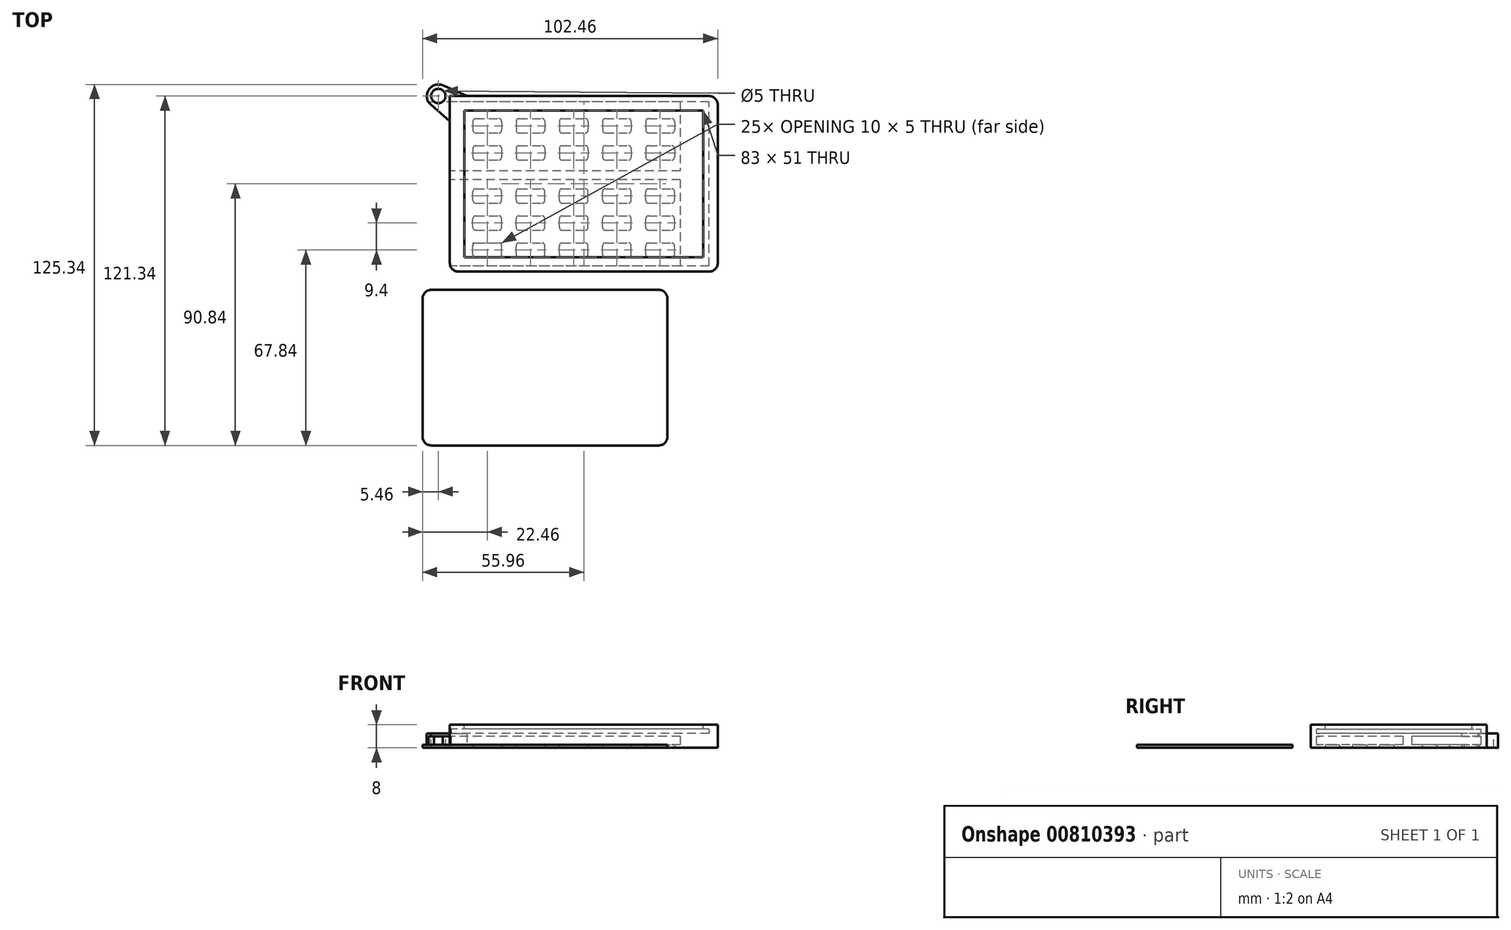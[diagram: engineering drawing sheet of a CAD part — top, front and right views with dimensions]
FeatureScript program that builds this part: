
annotation { "Feature Type Name" : "Feature", "Feature Type Description" : "" }
export const myFeature = defineFeature(function(context is Context, id is Id, definition is map)
    precondition{}
    {
        {
            var Q0;
            Q0=qCreatedBy(makeId("Top.planeOp"),FACE);
            var sketch = newSketch(context, id + "F0", { "sketchPlane" : qUnion([Q0])});
            skLineSegment(sketch, "E0.bottom", {"start": v(0, 0) * mm, "end": v(93, 0) * mm});
            skLineSegment(sketch, "E0.top", {"start": v(0, 61) * mm, "end": v(93, 61) * mm});
            skLineSegment(sketch, "E0.left", {"start": v(0, 0) * mm, "end": v(0, 61) * mm});
            skLineSegment(sketch, "E0.right", {"start": v(93, 0) * mm, "end": v(93, 61) * mm});
            skSolve(sketch);
        }
        {
            var Q0;
            Q0 = qSketchRegion(id + "F0", true);
            extrude(context, id + "F1", {"entities" : qUnion([Q0]), "depth" : 8 * mm, "offsetDistance" : 25 * mm});
        }
        {
            var Q0;
            Q0=makeQuery(id+"F1.opExtrude","SWEPT_EDGE",EDGE,{"disambiguationData":[OSD([sQuery(id+"F0.wireOp",EDGE,"E0.bottom"),sQuery(id+"F0.wireOp",EDGE,"E0.right")])]});
            var Q1;
            Q1=makeQuery(id+"F1.opExtrude","SWEPT_EDGE",EDGE,{"disambiguationData":[OSD([sQuery(id+"F0.wireOp",EDGE,"E0.top"),sQuery(id+"F0.wireOp",EDGE,"E0.right")])]});
            var Q2;
            Q2=makeQuery(id+"F1.opExtrude","SWEPT_EDGE",EDGE,{"disambiguationData":[OSD([sQuery(id+"F0.wireOp",EDGE,"E0.bottom"),sQuery(id+"F0.wireOp",EDGE,"E0.left")])]});
            fillet(context, id + "F2", {"entities" : qUnion([Q0, Q1, Q2]), "radius" : 3 * mm, "tangentPropagation" : true, "allowEdgeOverflow" : false});
        }
        {
            var Q0;
            Q0=qCreatedBy(makeId("Right.planeOp"),FACE);
            var sketch = newSketch(context, id + "F3", { "sketchPlane" : qUnion([Q0])});
            skLineSegment(sketch, "E1.bottom", {"start": v(2, 6.5) * mm, "end": v(59, 6.5) * mm});
            skLineSegment(sketch, "E1.top", {"start": v(59, 5) * mm, "end": v(2, 5) * mm});
            skLineSegment(sketch, "E1.left", {"start": v(59, 6.5) * mm, "end": v(59, 5) * mm});
            skLineSegment(sketch, "E1.right", {"start": v(2, 6.5) * mm, "end": v(2, 5) * mm});
            skLineSegment(sketch, "E2", {"start": v(30.5, 26.88) * mm, "end": v(30.5, -6.88) * mm, "construction": true});
            skSolve(sketch);
        }
        {
            var Q0;
            Q0 = qSketchRegion(id + "F3", true);
            extrude(context, id + "F4", {"entities" : qUnion([Q0]), "operationType" : NewBodyOperationType.REMOVE, "depth" : 90 * mm, "offsetDistance" : 25 * mm});
        }
        {
            var Q0;
            Q0=makeQuery(id+"F1.opExtrude","CAP_FACE",FACE,{"disambiguationData":[OSD([sQuery(id+"F0.wireOp",EDGE,"E0.bottom"),sQuery(id+"F0.wireOp",EDGE,"E0.top"),sQuery(id+"F0.wireOp",EDGE,"E0.left"),sQuery(id+"F0.wireOp",EDGE,"E0.right")])],"isStart":false});
            var sketch = newSketch(context, id + "F5", { "sketchPlane" : qUnion([Q0])});
            skLineSegment(sketch, "E3.bottom", {"start": v(5, 56) * mm, "end": v(88, 56) * mm});
            skLineSegment(sketch, "E3.top", {"start": v(5, 5) * mm, "end": v(88, 5) * mm});
            skLineSegment(sketch, "E3.left", {"start": v(5, 56) * mm, "end": v(5, 5) * mm});
            skLineSegment(sketch, "E3.right", {"start": v(88, 56) * mm, "end": v(88, 5) * mm});
            skSolve(sketch);
        }
        {
            var Q0;
            Q0 = qSketchRegion(id + "F5", true);
            extrude(context, id + "F6", {"entities" : qUnion([Q0]), "operationType" : NewBodyOperationType.REMOVE, "endBound" : BoundingType.UP_TO_NEXT, "oppositeDirection" : true, "depth" : 25 * mm, "offsetDistance" : 25 * mm, "hasSecondDirection" : true, "secondDirectionOppositeDirection" : false, "secondDirectionDepth" : 25 * mm});
        }
        {
            var Q0;
            Q0=makeQuery(id+"F1.opExtrude","SWEPT_FACE",FACE,{"disambiguationData":[OSD([sQuery(id+"F0.wireOp",EDGE,"E0.left")])]});
            var sketch = newSketch(context, id + "F7", { "sketchPlane" : qUnion([Q0])});
            skLineSegment(sketch, "E4.bottom", {"start": v(-32, 4) * mm, "end": v(-2, 4) * mm});
            skLineSegment(sketch, "E4.top", {"start": v(-32, 1) * mm, "end": v(-2, 1) * mm});
            skLineSegment(sketch, "E4.left", {"start": v(-32, 4) * mm, "end": v(-32, 1) * mm});
            skLineSegment(sketch, "E4.right", {"start": v(-2, 4) * mm, "end": v(-2, 1) * mm});
            skLineSegment(sketch, "E5.bottom", {"start": v(-59, 4) * mm, "end": v(-35, 4) * mm});
            skLineSegment(sketch, "E5.top", {"start": v(-59, 1) * mm, "end": v(-35, 1) * mm});
            skLineSegment(sketch, "E5.left", {"start": v(-59, 4) * mm, "end": v(-59, 1) * mm});
            skLineSegment(sketch, "E5.right", {"start": v(-35, 4) * mm, "end": v(-35, 1) * mm});
            skSolve(sketch);
        }
        {
            var Q0;
            Q0 = qSketchRegion(id + "F7", true);
            extrude(context, id + "F8", {"entities" : qUnion([Q0]), "operationType" : NewBodyOperationType.REMOVE, "oppositeDirection" : true, "depth" : 80 * mm, "offsetDistance" : 25 * mm});
        }
        {
            var Q0;
            Q0=makeQuery(id+"F1.opExtrude","CAP_FACE",FACE,{"disambiguationData":[OSD([sQuery(id+"F0.wireOp",EDGE,"E0.bottom"),sQuery(id+"F0.wireOp",EDGE,"E0.top"),sQuery(id+"F0.wireOp",EDGE,"E0.left"),sQuery(id+"F0.wireOp",EDGE,"E0.right")])],"isStart":true});
            var sketch = newSketch(context, id + "F9", { "sketchPlane" : qUnion([Q0])});
            skLineSegment(sketch, "E6.bottom", {"start": v(9, -5) * mm, "end": v(17, -5) * mm});
            skLineSegment(sketch, "E6.top", {"start": v(9, -10) * mm, "end": v(17, -10) * mm});
            skLineSegment(sketch, "E6.left", {"start": v(8, -6) * mm, "end": v(8, -9) * mm});
            skLineSegment(sketch, "E6.right", {"start": v(18, -6) * mm, "end": v(18, -9) * mm});
            skLineSegment(sketch, "E7", {"start": v(46.5, 0) * mm, "end": v(46.5, -63.42) * mm, "construction": true});
            skPoint(sketch, "E8.visualSharp", {"position": v(18, -10) * mm});
            skArc(sketch, "E8.filletArc", {"start": v(17, -10) * mm, "mid": v(17.7, -9.7) * mm, "end": v(18, -9) * mm});
            skPoint(sketch, "E9.visualSharp", {"position": v(18, -5) * mm});
            skArc(sketch, "E9.filletArc", {"start": v(18, -6) * mm, "mid": v(17.7, -5.3) * mm, "end": v(17, -5) * mm});
            skPoint(sketch, "E10.visualSharp", {"position": v(8, -10) * mm});
            skArc(sketch, "E10.filletArc", {"start": v(8, -9) * mm, "mid": v(8.3, -9.7) * mm, "end": v(9, -10) * mm});
            skPoint(sketch, "E11.visualSharp", {"position": v(8, -5) * mm});
            skArc(sketch, "E11.filletArc", {"start": v(9, -5) * mm, "mid": v(8.3, -5.3) * mm, "end": v(8, -6) * mm});
            skPoint(sketch, "E12.0.1.0", {"position": v(8, -14.4) * mm});
            skLineSegment(sketch, "E12.0.1.1", {"start": v(9, -14.4) * mm, "end": v(17, -14.4) * mm});
            skPoint(sketch, "E12.0.1.2", {"position": v(8, -19.4) * mm});
            skLineSegment(sketch, "E12.0.1.3", {"start": v(8, -15.4) * mm, "end": v(8, -18.4) * mm});
            skPoint(sketch, "E12.0.1.4", {"position": v(18, -19.4) * mm});
            skLineSegment(sketch, "E12.0.1.5", {"start": v(9, -19.4) * mm, "end": v(17, -19.4) * mm});
            skPoint(sketch, "E12.0.1.6", {"position": v(18, -14.4) * mm});
            skLineSegment(sketch, "E12.0.1.7", {"start": v(18, -15.4) * mm, "end": v(18, -18.4) * mm});
            skArc(sketch, "E12.0.1.8", {"start": v(17, -19.4) * mm, "mid": v(17.7, -19.1) * mm, "end": v(18, -18.4) * mm});
            skArc(sketch, "E12.0.1.9", {"start": v(9, -14.4) * mm, "mid": v(8.3, -14.7) * mm, "end": v(8, -15.4) * mm});
            skArc(sketch, "E12.0.1.10", {"start": v(18, -15.4) * mm, "mid": v(17.7, -14.7) * mm, "end": v(17, -14.4) * mm});
            skArc(sketch, "E12.0.1.11", {"start": v(8, -18.4) * mm, "mid": v(8.3, -19.1) * mm, "end": v(9, -19.4) * mm});
            skPoint(sketch, "E12.0.2.0", {"position": v(8, -23.8) * mm});
            skLineSegment(sketch, "E12.0.2.1", {"start": v(9, -23.8) * mm, "end": v(17, -23.8) * mm});
            skPoint(sketch, "E12.0.2.2", {"position": v(8, -28.8) * mm});
            skLineSegment(sketch, "E12.0.2.3", {"start": v(8, -24.8) * mm, "end": v(8, -27.8) * mm});
            skPoint(sketch, "E12.0.2.4", {"position": v(18, -28.8) * mm});
            skLineSegment(sketch, "E12.0.2.5", {"start": v(9, -28.8) * mm, "end": v(17, -28.8) * mm});
            skPoint(sketch, "E12.0.2.6", {"position": v(18, -23.8) * mm});
            skLineSegment(sketch, "E12.0.2.7", {"start": v(18, -24.8) * mm, "end": v(18, -27.8) * mm});
            skArc(sketch, "E12.0.2.8", {"start": v(17, -28.8) * mm, "mid": v(17.7, -28.5) * mm, "end": v(18, -27.8) * mm});
            skArc(sketch, "E12.0.2.9", {"start": v(9, -23.8) * mm, "mid": v(8.3, -24.1) * mm, "end": v(8, -24.8) * mm});
            skArc(sketch, "E12.0.2.10", {"start": v(18, -24.8) * mm, "mid": v(17.7, -24.1) * mm, "end": v(17, -23.8) * mm});
            skArc(sketch, "E12.0.2.11", {"start": v(8, -27.8) * mm, "mid": v(8.3, -28.5) * mm, "end": v(9, -28.8) * mm});
            skPoint(sketch, "E12.1.0.0", {"position": v(23, -5) * mm});
            skLineSegment(sketch, "E12.1.0.1", {"start": v(24, -5) * mm, "end": v(32, -5) * mm});
            skPoint(sketch, "E12.1.0.2", {"position": v(23, -10) * mm});
            skLineSegment(sketch, "E12.1.0.3", {"start": v(23, -6) * mm, "end": v(23, -9) * mm});
            skPoint(sketch, "E12.1.0.4", {"position": v(33, -10) * mm});
            skLineSegment(sketch, "E12.1.0.5", {"start": v(24, -10) * mm, "end": v(32, -10) * mm});
            skPoint(sketch, "E12.1.0.6", {"position": v(33, -5) * mm});
            skLineSegment(sketch, "E12.1.0.7", {"start": v(33, -6) * mm, "end": v(33, -9) * mm});
            skArc(sketch, "E12.1.0.8", {"start": v(32, -10) * mm, "mid": v(32.7, -9.7) * mm, "end": v(33, -9) * mm});
            skArc(sketch, "E12.1.0.9", {"start": v(24, -5) * mm, "mid": v(23.3, -5.3) * mm, "end": v(23, -6) * mm});
            skArc(sketch, "E12.1.0.10", {"start": v(33, -6) * mm, "mid": v(32.7, -5.3) * mm, "end": v(32, -5) * mm});
            skArc(sketch, "E12.1.0.11", {"start": v(23, -9) * mm, "mid": v(23.3, -9.7) * mm, "end": v(24, -10) * mm});
            skPoint(sketch, "E12.1.1.0", {"position": v(23, -14.4) * mm});
            skLineSegment(sketch, "E12.1.1.1", {"start": v(24, -14.4) * mm, "end": v(32, -14.4) * mm});
            skPoint(sketch, "E12.1.1.2", {"position": v(23, -19.4) * mm});
            skLineSegment(sketch, "E12.1.1.3", {"start": v(23, -15.4) * mm, "end": v(23, -18.4) * mm});
            skPoint(sketch, "E12.1.1.4", {"position": v(33, -19.4) * mm});
            skLineSegment(sketch, "E12.1.1.5", {"start": v(24, -19.4) * mm, "end": v(32, -19.4) * mm});
            skPoint(sketch, "E12.1.1.6", {"position": v(33, -14.4) * mm});
            skLineSegment(sketch, "E12.1.1.7", {"start": v(33, -15.4) * mm, "end": v(33, -18.4) * mm});
            skArc(sketch, "E12.1.1.8", {"start": v(32, -19.4) * mm, "mid": v(32.7, -19.1) * mm, "end": v(33, -18.4) * mm});
            skArc(sketch, "E12.1.1.9", {"start": v(24, -14.4) * mm, "mid": v(23.3, -14.7) * mm, "end": v(23, -15.4) * mm});
            skArc(sketch, "E12.1.1.10", {"start": v(33, -15.4) * mm, "mid": v(32.7, -14.7) * mm, "end": v(32, -14.4) * mm});
            skArc(sketch, "E12.1.1.11", {"start": v(23, -18.4) * mm, "mid": v(23.3, -19.1) * mm, "end": v(24, -19.4) * mm});
            skPoint(sketch, "E12.1.2.0", {"position": v(23, -23.8) * mm});
            skLineSegment(sketch, "E12.1.2.1", {"start": v(24, -23.8) * mm, "end": v(32, -23.8) * mm});
            skPoint(sketch, "E12.1.2.2", {"position": v(23, -28.8) * mm});
            skLineSegment(sketch, "E12.1.2.3", {"start": v(23, -24.8) * mm, "end": v(23, -27.8) * mm});
            skPoint(sketch, "E12.1.2.4", {"position": v(33, -28.8) * mm});
            skLineSegment(sketch, "E12.1.2.5", {"start": v(24, -28.8) * mm, "end": v(32, -28.8) * mm});
            skPoint(sketch, "E12.1.2.6", {"position": v(33, -23.8) * mm});
            skLineSegment(sketch, "E12.1.2.7", {"start": v(33, -24.8) * mm, "end": v(33, -27.8) * mm});
            skArc(sketch, "E12.1.2.8", {"start": v(32, -28.8) * mm, "mid": v(32.7, -28.5) * mm, "end": v(33, -27.8) * mm});
            skArc(sketch, "E12.1.2.9", {"start": v(24, -23.8) * mm, "mid": v(23.3, -24.1) * mm, "end": v(23, -24.8) * mm});
            skArc(sketch, "E12.1.2.10", {"start": v(33, -24.8) * mm, "mid": v(32.7, -24.1) * mm, "end": v(32, -23.8) * mm});
            skArc(sketch, "E12.1.2.11", {"start": v(23, -27.8) * mm, "mid": v(23.3, -28.5) * mm, "end": v(24, -28.8) * mm});
            skPoint(sketch, "E12.2.0.0", {"position": v(38, -5) * mm});
            skLineSegment(sketch, "E12.2.0.1", {"start": v(39, -5) * mm, "end": v(47, -5) * mm});
            skPoint(sketch, "E12.2.0.2", {"position": v(38, -10) * mm});
            skLineSegment(sketch, "E12.2.0.3", {"start": v(38, -6) * mm, "end": v(38, -9) * mm});
            skPoint(sketch, "E12.2.0.4", {"position": v(48, -10) * mm});
            skLineSegment(sketch, "E12.2.0.5", {"start": v(39, -10) * mm, "end": v(47, -10) * mm});
            skPoint(sketch, "E12.2.0.6", {"position": v(48, -5) * mm});
            skLineSegment(sketch, "E12.2.0.7", {"start": v(48, -6) * mm, "end": v(48, -9) * mm});
            skArc(sketch, "E12.2.0.8", {"start": v(47, -10) * mm, "mid": v(47.7, -9.7) * mm, "end": v(48, -9) * mm});
            skArc(sketch, "E12.2.0.9", {"start": v(39, -5) * mm, "mid": v(38.3, -5.3) * mm, "end": v(38, -6) * mm});
            skArc(sketch, "E12.2.0.10", {"start": v(48, -6) * mm, "mid": v(47.7, -5.3) * mm, "end": v(47, -5) * mm});
            skArc(sketch, "E12.2.0.11", {"start": v(38, -9) * mm, "mid": v(38.3, -9.7) * mm, "end": v(39, -10) * mm});
            skPoint(sketch, "E12.2.1.0", {"position": v(38, -14.4) * mm});
            skLineSegment(sketch, "E12.2.1.1", {"start": v(39, -14.4) * mm, "end": v(47, -14.4) * mm});
            skPoint(sketch, "E12.2.1.2", {"position": v(38, -19.4) * mm});
            skLineSegment(sketch, "E12.2.1.3", {"start": v(38, -15.4) * mm, "end": v(38, -18.4) * mm});
            skPoint(sketch, "E12.2.1.4", {"position": v(48, -19.4) * mm});
            skLineSegment(sketch, "E12.2.1.5", {"start": v(39, -19.4) * mm, "end": v(47, -19.4) * mm});
            skPoint(sketch, "E12.2.1.6", {"position": v(48, -14.4) * mm});
            skLineSegment(sketch, "E12.2.1.7", {"start": v(48, -15.4) * mm, "end": v(48, -18.4) * mm});
            skArc(sketch, "E12.2.1.8", {"start": v(47, -19.4) * mm, "mid": v(47.7, -19.1) * mm, "end": v(48, -18.4) * mm});
            skArc(sketch, "E12.2.1.9", {"start": v(39, -14.4) * mm, "mid": v(38.3, -14.7) * mm, "end": v(38, -15.4) * mm});
            skArc(sketch, "E12.2.1.10", {"start": v(48, -15.4) * mm, "mid": v(47.7, -14.7) * mm, "end": v(47, -14.4) * mm});
            skArc(sketch, "E12.2.1.11", {"start": v(38, -18.4) * mm, "mid": v(38.3, -19.1) * mm, "end": v(39, -19.4) * mm});
            skPoint(sketch, "E12.2.2.0", {"position": v(38, -23.8) * mm});
            skLineSegment(sketch, "E12.2.2.1", {"start": v(39, -23.8) * mm, "end": v(47, -23.8) * mm});
            skPoint(sketch, "E12.2.2.2", {"position": v(38, -28.8) * mm});
            skLineSegment(sketch, "E12.2.2.3", {"start": v(38, -24.8) * mm, "end": v(38, -27.8) * mm});
            skPoint(sketch, "E12.2.2.4", {"position": v(48, -28.8) * mm});
            skLineSegment(sketch, "E12.2.2.5", {"start": v(39, -28.8) * mm, "end": v(47, -28.8) * mm});
            skPoint(sketch, "E12.2.2.6", {"position": v(48, -23.8) * mm});
            skLineSegment(sketch, "E12.2.2.7", {"start": v(48, -24.8) * mm, "end": v(48, -27.8) * mm});
            skArc(sketch, "E12.2.2.8", {"start": v(47, -28.8) * mm, "mid": v(47.7, -28.5) * mm, "end": v(48, -27.8) * mm});
            skArc(sketch, "E12.2.2.9", {"start": v(39, -23.8) * mm, "mid": v(38.3, -24.1) * mm, "end": v(38, -24.8) * mm});
            skArc(sketch, "E12.2.2.10", {"start": v(48, -24.8) * mm, "mid": v(47.7, -24.1) * mm, "end": v(47, -23.8) * mm});
            skArc(sketch, "E12.2.2.11", {"start": v(38, -27.8) * mm, "mid": v(38.3, -28.5) * mm, "end": v(39, -28.8) * mm});
            skPoint(sketch, "E12.3.0.0", {"position": v(53, -5) * mm});
            skLineSegment(sketch, "E12.3.0.1", {"start": v(54, -5) * mm, "end": v(62, -5) * mm});
            skPoint(sketch, "E12.3.0.2", {"position": v(53, -10) * mm});
            skLineSegment(sketch, "E12.3.0.3", {"start": v(53, -6) * mm, "end": v(53, -9) * mm});
            skPoint(sketch, "E12.3.0.4", {"position": v(63, -10) * mm});
            skLineSegment(sketch, "E12.3.0.5", {"start": v(54, -10) * mm, "end": v(62, -10) * mm});
            skPoint(sketch, "E12.3.0.6", {"position": v(63, -5) * mm});
            skLineSegment(sketch, "E12.3.0.7", {"start": v(63, -6) * mm, "end": v(63, -9) * mm});
            skArc(sketch, "E12.3.0.8", {"start": v(62, -10) * mm, "mid": v(62.7, -9.7) * mm, "end": v(63, -9) * mm});
            skArc(sketch, "E12.3.0.9", {"start": v(54, -5) * mm, "mid": v(53.3, -5.3) * mm, "end": v(53, -6) * mm});
            skArc(sketch, "E12.3.0.10", {"start": v(63, -6) * mm, "mid": v(62.7, -5.3) * mm, "end": v(62, -5) * mm});
            skArc(sketch, "E12.3.0.11", {"start": v(53, -9) * mm, "mid": v(53.3, -9.7) * mm, "end": v(54, -10) * mm});
            skPoint(sketch, "E12.3.1.0", {"position": v(53, -14.4) * mm});
            skLineSegment(sketch, "E12.3.1.1", {"start": v(54, -14.4) * mm, "end": v(62, -14.4) * mm});
            skPoint(sketch, "E12.3.1.2", {"position": v(53, -19.4) * mm});
            skLineSegment(sketch, "E12.3.1.3", {"start": v(53, -15.4) * mm, "end": v(53, -18.4) * mm});
            skPoint(sketch, "E12.3.1.4", {"position": v(63, -19.4) * mm});
            skLineSegment(sketch, "E12.3.1.5", {"start": v(54, -19.4) * mm, "end": v(62, -19.4) * mm});
            skPoint(sketch, "E12.3.1.6", {"position": v(63, -14.4) * mm});
            skLineSegment(sketch, "E12.3.1.7", {"start": v(63, -15.4) * mm, "end": v(63, -18.4) * mm});
            skArc(sketch, "E12.3.1.8", {"start": v(62, -19.4) * mm, "mid": v(62.7, -19.1) * mm, "end": v(63, -18.4) * mm});
            skArc(sketch, "E12.3.1.9", {"start": v(54, -14.4) * mm, "mid": v(53.3, -14.7) * mm, "end": v(53, -15.4) * mm});
            skArc(sketch, "E12.3.1.10", {"start": v(63, -15.4) * mm, "mid": v(62.7, -14.7) * mm, "end": v(62, -14.4) * mm});
            skArc(sketch, "E12.3.1.11", {"start": v(53, -18.4) * mm, "mid": v(53.3, -19.1) * mm, "end": v(54, -19.4) * mm});
            skPoint(sketch, "E12.3.2.0", {"position": v(53, -23.8) * mm});
            skLineSegment(sketch, "E12.3.2.1", {"start": v(54, -23.8) * mm, "end": v(62, -23.8) * mm});
            skPoint(sketch, "E12.3.2.2", {"position": v(53, -28.8) * mm});
            skLineSegment(sketch, "E12.3.2.3", {"start": v(53, -24.8) * mm, "end": v(53, -27.8) * mm});
            skPoint(sketch, "E12.3.2.4", {"position": v(63, -28.8) * mm});
            skLineSegment(sketch, "E12.3.2.5", {"start": v(54, -28.8) * mm, "end": v(62, -28.8) * mm});
            skPoint(sketch, "E12.3.2.6", {"position": v(63, -23.8) * mm});
            skLineSegment(sketch, "E12.3.2.7", {"start": v(63, -24.8) * mm, "end": v(63, -27.8) * mm});
            skArc(sketch, "E12.3.2.8", {"start": v(62, -28.8) * mm, "mid": v(62.7, -28.5) * mm, "end": v(63, -27.8) * mm});
            skArc(sketch, "E12.3.2.9", {"start": v(54, -23.8) * mm, "mid": v(53.3, -24.1) * mm, "end": v(53, -24.8) * mm});
            skArc(sketch, "E12.3.2.10", {"start": v(63, -24.8) * mm, "mid": v(62.7, -24.1) * mm, "end": v(62, -23.8) * mm});
            skArc(sketch, "E12.3.2.11", {"start": v(53, -27.8) * mm, "mid": v(53.3, -28.5) * mm, "end": v(54, -28.8) * mm});
            skPoint(sketch, "E12.4.0.0", {"position": v(68, -5) * mm});
            skLineSegment(sketch, "E12.4.0.1", {"start": v(69, -5) * mm, "end": v(77, -5) * mm});
            skPoint(sketch, "E12.4.0.2", {"position": v(68, -10) * mm});
            skLineSegment(sketch, "E12.4.0.3", {"start": v(68, -6) * mm, "end": v(68, -9) * mm});
            skPoint(sketch, "E12.4.0.4", {"position": v(78, -10) * mm});
            skLineSegment(sketch, "E12.4.0.5", {"start": v(69, -10) * mm, "end": v(77, -10) * mm});
            skPoint(sketch, "E12.4.0.6", {"position": v(78, -5) * mm});
            skLineSegment(sketch, "E12.4.0.7", {"start": v(78, -6) * mm, "end": v(78, -9) * mm});
            skArc(sketch, "E12.4.0.8", {"start": v(77, -10) * mm, "mid": v(77.7, -9.7) * mm, "end": v(78, -9) * mm});
            skArc(sketch, "E12.4.0.9", {"start": v(69, -5) * mm, "mid": v(68.3, -5.3) * mm, "end": v(68, -6) * mm});
            skArc(sketch, "E12.4.0.10", {"start": v(78, -6) * mm, "mid": v(77.7, -5.3) * mm, "end": v(77, -5) * mm});
            skArc(sketch, "E12.4.0.11", {"start": v(68, -9) * mm, "mid": v(68.3, -9.7) * mm, "end": v(69, -10) * mm});
            skPoint(sketch, "E12.4.1.0", {"position": v(68, -14.4) * mm});
            skLineSegment(sketch, "E12.4.1.1", {"start": v(69, -14.4) * mm, "end": v(77, -14.4) * mm});
            skPoint(sketch, "E12.4.1.2", {"position": v(68, -19.4) * mm});
            skLineSegment(sketch, "E12.4.1.3", {"start": v(68, -15.4) * mm, "end": v(68, -18.4) * mm});
            skPoint(sketch, "E12.4.1.4", {"position": v(78, -19.4) * mm});
            skLineSegment(sketch, "E12.4.1.5", {"start": v(69, -19.4) * mm, "end": v(77, -19.4) * mm});
            skPoint(sketch, "E12.4.1.6", {"position": v(78, -14.4) * mm});
            skLineSegment(sketch, "E12.4.1.7", {"start": v(78, -15.4) * mm, "end": v(78, -18.4) * mm});
            skArc(sketch, "E12.4.1.8", {"start": v(77, -19.4) * mm, "mid": v(77.7, -19.1) * mm, "end": v(78, -18.4) * mm});
            skArc(sketch, "E12.4.1.9", {"start": v(69, -14.4) * mm, "mid": v(68.3, -14.7) * mm, "end": v(68, -15.4) * mm});
            skArc(sketch, "E12.4.1.10", {"start": v(78, -15.4) * mm, "mid": v(77.7, -14.7) * mm, "end": v(77, -14.4) * mm});
            skArc(sketch, "E12.4.1.11", {"start": v(68, -18.4) * mm, "mid": v(68.3, -19.1) * mm, "end": v(69, -19.4) * mm});
            skPoint(sketch, "E12.4.2.0", {"position": v(68, -23.8) * mm});
            skLineSegment(sketch, "E12.4.2.1", {"start": v(69, -23.8) * mm, "end": v(77, -23.8) * mm});
            skPoint(sketch, "E12.4.2.2", {"position": v(68, -28.8) * mm});
            skLineSegment(sketch, "E12.4.2.3", {"start": v(68, -24.8) * mm, "end": v(68, -27.8) * mm});
            skPoint(sketch, "E12.4.2.4", {"position": v(78, -28.8) * mm});
            skLineSegment(sketch, "E12.4.2.5", {"start": v(69, -28.8) * mm, "end": v(77, -28.8) * mm});
            skPoint(sketch, "E12.4.2.6", {"position": v(78, -23.8) * mm});
            skLineSegment(sketch, "E12.4.2.7", {"start": v(78, -24.8) * mm, "end": v(78, -27.8) * mm});
            skArc(sketch, "E12.4.2.8", {"start": v(77, -28.8) * mm, "mid": v(77.7, -28.5) * mm, "end": v(78, -27.8) * mm});
            skArc(sketch, "E12.4.2.9", {"start": v(69, -23.8) * mm, "mid": v(68.3, -24.1) * mm, "end": v(68, -24.8) * mm});
            skArc(sketch, "E12.4.2.10", {"start": v(78, -24.8) * mm, "mid": v(77.7, -24.1) * mm, "end": v(77, -23.8) * mm});
            skArc(sketch, "E12.4.2.11", {"start": v(68, -27.8) * mm, "mid": v(68.3, -28.5) * mm, "end": v(69, -28.8) * mm});
            skLineSegment(sketch, "E12.direction1", {"start": v(8, -10) * mm, "end": v(23, -10) * mm, "construction": true});
            skLineSegment(sketch, "E12.direction2", {"start": v(8, -10) * mm, "end": v(8, -19.4) * mm, "construction": true});
            skLineSegment(sketch, "E13", {"start": v(0, -33.78) * mm, "end": v(93, -33.78) * mm, "construction": true});
            skLineSegment(sketch, "E14.MirrorCS", {"start": v(23, -52.16) * mm, "end": v(23, -49.16) * mm});
            skArc(sketch, "E15.MirrorCS", {"start": v(78, -52.16) * mm, "mid": v(77.7, -52.86) * mm, "end": v(77, -53.16) * mm});
            skArc(sketch, "E16.MirrorCS", {"start": v(48, -52.16) * mm, "mid": v(47.7, -52.86) * mm, "end": v(47, -53.16) * mm});
            skArc(sketch, "E17.MirrorCS", {"start": v(69, -53.16) * mm, "mid": v(68.3, -52.86) * mm, "end": v(68, -52.16) * mm});
            skArc(sketch, "E18.MirrorCS", {"start": v(39, -53.16) * mm, "mid": v(38.3, -52.86) * mm, "end": v(38, -52.16) * mm});
            skArc(sketch, "E19.MirrorCS", {"start": v(62, -38.76) * mm, "mid": v(62.7, -39.05) * mm, "end": v(63, -39.76) * mm});
            skLineSegment(sketch, "E20.MirrorCS", {"start": v(8, -52.16) * mm, "end": v(8, -49.16) * mm});
            skArc(sketch, "E21.MirrorCS", {"start": v(9, -53.16) * mm, "mid": v(8.3, -52.86) * mm, "end": v(8, -52.16) * mm});
            skArc(sketch, "E22.MirrorCS", {"start": v(24, -53.16) * mm, "mid": v(23.3, -52.86) * mm, "end": v(23, -52.16) * mm});
            skArc(sketch, "E23.MirrorCS", {"start": v(9, -43.76) * mm, "mid": v(8.3, -43.46) * mm, "end": v(8, -42.76) * mm});
            skLineSegment(sketch, "E24.MirrorCS", {"start": v(68, -42.76) * mm, "end": v(68, -39.76) * mm});
            skLineSegment(sketch, "E25.MirrorCS", {"start": v(38, -42.76) * mm, "end": v(38, -39.76) * mm});
            skLineSegment(sketch, "E26.MirrorCS", {"start": v(53, -52.16) * mm, "end": v(53, -49.16) * mm});
            skLineSegment(sketch, "E27.MirrorCS", {"start": v(8, -42.76) * mm, "end": v(8, -39.76) * mm});
            skArc(sketch, "E28.MirrorCS", {"start": v(53, -39.76) * mm, "mid": v(53.3, -39.05) * mm, "end": v(54, -38.76) * mm});
            skArc(sketch, "E29.MirrorCS", {"start": v(68, -49.16) * mm, "mid": v(68.3, -48.45) * mm, "end": v(69, -48.16) * mm});
            skArc(sketch, "E30.MirrorCS", {"start": v(38, -49.16) * mm, "mid": v(38.3, -48.45) * mm, "end": v(39, -48.16) * mm});
            skArc(sketch, "E31.MirrorCS", {"start": v(23, -39.76) * mm, "mid": v(23.3, -39.05) * mm, "end": v(24, -38.76) * mm});
            skArc(sketch, "E32.MirrorCS", {"start": v(8, -49.16) * mm, "mid": v(8.3, -48.45) * mm, "end": v(9, -48.16) * mm});
            skArc(sketch, "E33.MirrorCS", {"start": v(63, -42.76) * mm, "mid": v(62.7, -43.46) * mm, "end": v(62, -43.76) * mm});
            skArc(sketch, "E34.MirrorCS", {"start": v(33, -42.76) * mm, "mid": v(32.7, -43.46) * mm, "end": v(32, -43.76) * mm});
            skArc(sketch, "E35.MirrorCS", {"start": v(54, -43.76) * mm, "mid": v(53.3, -43.46) * mm, "end": v(53, -42.76) * mm});
            skArc(sketch, "E36.MirrorCS", {"start": v(24, -43.76) * mm, "mid": v(23.3, -43.46) * mm, "end": v(23, -42.76) * mm});
            skLineSegment(sketch, "E37.MirrorCS", {"start": v(63, -42.76) * mm, "end": v(63, -39.76) * mm});
            skLineSegment(sketch, "E38.MirrorCS", {"start": v(78, -52.16) * mm, "end": v(78, -49.16) * mm});
            skLineSegment(sketch, "E39.MirrorCS", {"start": v(33, -42.76) * mm, "end": v(33, -39.76) * mm});
            skLineSegment(sketch, "E40.MirrorCS", {"start": v(48, -52.16) * mm, "end": v(48, -49.16) * mm});
            skArc(sketch, "E41.MirrorCS", {"start": v(32, -38.76) * mm, "mid": v(32.7, -39.05) * mm, "end": v(33, -39.76) * mm});
            skArc(sketch, "E42.MirrorCS", {"start": v(47, -48.16) * mm, "mid": v(47.7, -48.45) * mm, "end": v(48, -49.16) * mm});
            skArc(sketch, "E43.MirrorCS", {"start": v(77, -48.16) * mm, "mid": v(77.7, -48.45) * mm, "end": v(78, -49.16) * mm});
            skLineSegment(sketch, "E44.MirrorCS", {"start": v(18, -52.16) * mm, "end": v(18, -49.16) * mm});
            skLineSegment(sketch, "E45.MirrorCS", {"start": v(53, -42.76) * mm, "end": v(53, -39.76) * mm});
            skLineSegment(sketch, "E46.MirrorCS", {"start": v(68, -52.16) * mm, "end": v(68, -49.16) * mm});
            skLineSegment(sketch, "E47.MirrorCS", {"start": v(8, -57.56) * mm, "end": v(8, -48.16) * mm, "construction": true});
            skArc(sketch, "E48.MirrorCS", {"start": v(18, -52.16) * mm, "mid": v(17.7, -52.86) * mm, "end": v(17, -53.16) * mm});
            skArc(sketch, "E49.MirrorCS", {"start": v(17, -48.16) * mm, "mid": v(17.7, -48.45) * mm, "end": v(18, -49.16) * mm});
            skLineSegment(sketch, "E50.MirrorCS", {"start": v(23, -42.76) * mm, "end": v(23, -39.76) * mm});
            skLineSegment(sketch, "E51.MirrorCS", {"start": v(38, -52.16) * mm, "end": v(38, -49.16) * mm});
            skArc(sketch, "E52.MirrorCS", {"start": v(38, -39.76) * mm, "mid": v(38.3, -39.05) * mm, "end": v(39, -38.76) * mm});
            skArc(sketch, "E53.MirrorCS", {"start": v(53, -49.16) * mm, "mid": v(53.3, -48.45) * mm, "end": v(54, -48.16) * mm});
            skArc(sketch, "E54.MirrorCS", {"start": v(68, -39.76) * mm, "mid": v(68.3, -39.05) * mm, "end": v(69, -38.76) * mm});
            skArc(sketch, "E55.MirrorCS", {"start": v(23, -49.16) * mm, "mid": v(23.3, -48.45) * mm, "end": v(24, -48.16) * mm});
            skArc(sketch, "E56.MirrorCS", {"start": v(8, -39.76) * mm, "mid": v(8.3, -39.05) * mm, "end": v(9, -38.76) * mm});
            skArc(sketch, "E57.MirrorCS", {"start": v(54, -53.16) * mm, "mid": v(53.3, -52.86) * mm, "end": v(53, -52.16) * mm});
            skArc(sketch, "E58.MirrorCS", {"start": v(77, -38.76) * mm, "mid": v(77.7, -39.05) * mm, "end": v(78, -39.76) * mm});
            skArc(sketch, "E59.MirrorCS", {"start": v(32, -48.16) * mm, "mid": v(32.7, -48.45) * mm, "end": v(33, -49.16) * mm});
            skLineSegment(sketch, "E60.MirrorCS", {"start": v(33, -52.16) * mm, "end": v(33, -49.16) * mm});
            skLineSegment(sketch, "E61.MirrorCS", {"start": v(63, -52.16) * mm, "end": v(63, -49.16) * mm});
            skLineSegment(sketch, "E62.MirrorCS", {"start": v(78, -42.76) * mm, "end": v(78, -39.76) * mm});
            skArc(sketch, "E63.MirrorCS", {"start": v(39, -43.76) * mm, "mid": v(38.3, -43.46) * mm, "end": v(38, -42.76) * mm});
            skArc(sketch, "E64.MirrorCS", {"start": v(47, -38.76) * mm, "mid": v(47.7, -39.05) * mm, "end": v(48, -39.76) * mm});
            skArc(sketch, "E65.MirrorCS", {"start": v(69, -43.76) * mm, "mid": v(68.3, -43.46) * mm, "end": v(68, -42.76) * mm});
            skLineSegment(sketch, "E66.MirrorCS", {"start": v(18, -42.76) * mm, "end": v(18, -39.76) * mm});
            skArc(sketch, "E67.MirrorCS", {"start": v(17, -38.76) * mm, "mid": v(17.7, -39.05) * mm, "end": v(18, -39.76) * mm});
            skArc(sketch, "E68.MirrorCS", {"start": v(63, -52.16) * mm, "mid": v(62.7, -52.86) * mm, "end": v(62, -53.16) * mm});
            skArc(sketch, "E69.MirrorCS", {"start": v(33, -52.16) * mm, "mid": v(32.7, -52.86) * mm, "end": v(32, -53.16) * mm});
            skArc(sketch, "E70.MirrorCS", {"start": v(18, -42.76) * mm, "mid": v(17.7, -43.46) * mm, "end": v(17, -43.76) * mm});
            skLineSegment(sketch, "E71.MirrorCS", {"start": v(48, -42.76) * mm, "end": v(48, -39.76) * mm});
            skArc(sketch, "E72.MirrorCS", {"start": v(48, -42.76) * mm, "mid": v(47.7, -43.46) * mm, "end": v(47, -43.76) * mm});
            skArc(sketch, "E73.MirrorCS", {"start": v(78, -42.76) * mm, "mid": v(77.7, -43.46) * mm, "end": v(77, -43.76) * mm});
            skArc(sketch, "E74.MirrorCS", {"start": v(62, -48.16) * mm, "mid": v(62.7, -48.45) * mm, "end": v(63, -49.16) * mm});
            skLineSegment(sketch, "E75.MirrorCS", {"start": v(24, -53.16) * mm, "end": v(32, -53.16) * mm});
            skPoint(sketch, "E76.MirrorP", {"position": v(8, -57.56) * mm});
            skPoint(sketch, "E77.MirrorP", {"position": v(23, -53.16) * mm});
            skPoint(sketch, "E78.MirrorP", {"position": v(18, -53.16) * mm});
            skLineSegment(sketch, "E79.MirrorCS", {"start": v(39, -38.76) * mm, "end": v(47, -38.76) * mm});
            skPoint(sketch, "E80.MirrorP", {"position": v(78, -48.16) * mm});
            skPoint(sketch, "E81.MirrorP", {"position": v(33, -38.76) * mm});
            skPoint(sketch, "E82.MirrorP", {"position": v(48, -48.16) * mm});
            skPoint(sketch, "E83.MirrorP", {"position": v(18, -48.16) * mm});
            skPoint(sketch, "E84.MirrorP", {"position": v(53, -38.76) * mm});
            skPoint(sketch, "E85.MirrorP", {"position": v(68, -48.16) * mm});
            skPoint(sketch, "E86.MirrorP", {"position": v(23, -38.76) * mm});
            skPoint(sketch, "E87.MirrorP", {"position": v(38, -48.16) * mm});
            skPoint(sketch, "E88.MirrorP", {"position": v(8, -48.16) * mm});
            skLineSegment(sketch, "E89.MirrorCS", {"start": v(69, -43.76) * mm, "end": v(77, -43.76) * mm});
            skLineSegment(sketch, "E90.MirrorCS", {"start": v(54, -53.16) * mm, "end": v(62, -53.16) * mm});
            skLineSegment(sketch, "E91.MirrorCS", {"start": v(39, -43.76) * mm, "end": v(47, -43.76) * mm});
            skLineSegment(sketch, "E92.MirrorCS", {"start": v(9, -43.76) * mm, "end": v(17, -43.76) * mm});
            skPoint(sketch, "E93.MirrorP", {"position": v(23, -43.76) * mm});
            skPoint(sketch, "E94.MirrorP", {"position": v(38, -53.16) * mm});
            skPoint(sketch, "E95.MirrorP", {"position": v(8, -53.16) * mm});
            skPoint(sketch, "E96.MirrorP", {"position": v(68, -53.16) * mm});
            skPoint(sketch, "E97.MirrorP", {"position": v(53, -43.76) * mm});
            skLineSegment(sketch, "E98.MirrorCS", {"start": v(69, -48.16) * mm, "end": v(77, -48.16) * mm});
            skLineSegment(sketch, "E99.MirrorCS", {"start": v(54, -38.76) * mm, "end": v(62, -38.76) * mm});
            skLineSegment(sketch, "E100.MirrorCS", {"start": v(24, -38.76) * mm, "end": v(32, -38.76) * mm});
            skLineSegment(sketch, "E101.MirrorCS", {"start": v(39, -48.16) * mm, "end": v(47, -48.16) * mm});
            skPoint(sketch, "E102.MirrorP", {"position": v(48, -43.76) * mm});
            skPoint(sketch, "E103.MirrorP", {"position": v(63, -53.16) * mm});
            skPoint(sketch, "E104.MirrorP", {"position": v(78, -43.76) * mm});
            skPoint(sketch, "E105.MirrorP", {"position": v(18, -43.76) * mm});
            skPoint(sketch, "E106.MirrorP", {"position": v(33, -53.16) * mm});
            skLineSegment(sketch, "E107.MirrorCS", {"start": v(9, -48.16) * mm, "end": v(17, -48.16) * mm});
            skLineSegment(sketch, "E108.MirrorCS", {"start": v(9, -53.16) * mm, "end": v(17, -53.16) * mm});
            skLineSegment(sketch, "E109.MirrorCS", {"start": v(46.5, -67.56) * mm, "end": v(46.5, -4.14) * mm, "construction": true});
            skPoint(sketch, "E110.MirrorP", {"position": v(48, -38.76) * mm});
            skPoint(sketch, "E111.MirrorP", {"position": v(63, -48.16) * mm});
            skPoint(sketch, "E112.MirrorP", {"position": v(78, -38.76) * mm});
            skPoint(sketch, "E113.MirrorP", {"position": v(33, -48.16) * mm});
            skPoint(sketch, "E114.MirrorP", {"position": v(18, -38.76) * mm});
            skLineSegment(sketch, "E115.MirrorCS", {"start": v(54, -43.76) * mm, "end": v(62, -43.76) * mm});
            skLineSegment(sketch, "E116.MirrorCS", {"start": v(69, -53.16) * mm, "end": v(77, -53.16) * mm});
            skLineSegment(sketch, "E117.MirrorCS", {"start": v(24, -43.76) * mm, "end": v(32, -43.76) * mm});
            skLineSegment(sketch, "E118.MirrorCS", {"start": v(39, -53.16) * mm, "end": v(47, -53.16) * mm});
            skPoint(sketch, "E119.MirrorP", {"position": v(68, -38.76) * mm});
            skPoint(sketch, "E120.MirrorP", {"position": v(8, -38.76) * mm});
            skPoint(sketch, "E121.MirrorP", {"position": v(23, -48.16) * mm});
            skPoint(sketch, "E122.MirrorP", {"position": v(53, -53.16) * mm});
            skPoint(sketch, "E123.MirrorP", {"position": v(38, -43.76) * mm});
            skPoint(sketch, "E124.MirrorP", {"position": v(68, -43.76) * mm});
            skLineSegment(sketch, "E125.MirrorCS", {"start": v(9, -38.76) * mm, "end": v(17, -38.76) * mm});
            skPoint(sketch, "E126.MirrorP", {"position": v(33, -43.76) * mm});
            skPoint(sketch, "E127.MirrorP", {"position": v(63, -38.76) * mm});
            skLineSegment(sketch, "E128.MirrorCS", {"start": v(69, -38.76) * mm, "end": v(77, -38.76) * mm});
            skPoint(sketch, "E129.MirrorP", {"position": v(53, -48.16) * mm});
            skLineSegment(sketch, "E130.MirrorCS", {"start": v(54, -48.16) * mm, "end": v(62, -48.16) * mm});
            skPoint(sketch, "E131.MirrorP", {"position": v(8, -43.76) * mm});
            skLineSegment(sketch, "E132.MirrorCS", {"start": v(24, -48.16) * mm, "end": v(32, -48.16) * mm});
            skPoint(sketch, "E133.MirrorP", {"position": v(48, -53.16) * mm});
            skPoint(sketch, "E134.MirrorP", {"position": v(63, -43.76) * mm});
            skPoint(sketch, "E135.MirrorP", {"position": v(38, -38.76) * mm});
            skPoint(sketch, "E136.MirrorP", {"position": v(78, -53.16) * mm});
            skSolve(sketch);
        }
        {
            var Q0;
            Q0 = qSketchRegion(id + "F9", true);
            extrude(context, id + "F10", {"entities" : qUnion([Q0]), "operationType" : NewBodyOperationType.REMOVE, "oppositeDirection" : true, "depth" : 2 * mm, "offsetDistance" : 25 * mm});
        }
        {
            var Q0;
            Q0=qCreatedBy(makeId("Top.planeOp"),FACE);
            var sketch = newSketch(context, id + "F11", { "sketchPlane" : qUnion([Q0])});
            skArc(sketch, "E137", {"start": v(-2.38, 64.66) * mm, "mid": v(-7.4, 63.1) * mm, "end": v(-6.55, 57.92) * mm});
            skLineSegment(sketch, "E138", {"start": v(14.45, 61) * mm, "end": v(-34.97, 61) * mm, "construction": true});
            skLineSegment(sketch, "E139", {"start": v(-2.38, 64.66) * mm, "end": v(5.86, 61) * mm});
            skLineSegment(sketch, "E140", {"start": v(-6.55, 57.92) * mm, "end": v(0, 52.25) * mm});
            skLineSegment(sketch, "E141", {"start": v(0, 52.25) * mm, "end": v(0.9, 60.19) * mm});
            skLineSegment(sketch, "E142", {"start": v(0.9, 60.19) * mm, "end": v(5.86, 61) * mm});
            skSolve(sketch);
        }
        {
            var Q0;
            Q0 = qSketchRegion(id + "F11", true);
            extrude(context, id + "F12", {"entities" : qUnion([Q0]), "operationType" : NewBodyOperationType.ADD, "depth" : 5 * mm, "offsetDistance" : 25 * mm});
        }
        {
            var Q0;
            Q0=makeQuery(id+"F12.boolean.opBoolean","MERGE",FACE,{"derivedFrom":[makeQuery(id+"F4.boolean.opBoolean","COPY",FACE,{"derivedFrom":makeQuery(id+"F4.opExtrude","SWEPT_FACE",FACE,{"disambiguationData":[OSD([sQuery(id+"F3.wireOp",EDGE,"E1.top")])]})}),makeQuery(id+"F12.opExtrude","CAP_FACE",FACE,{"disambiguationData":[OSD([sQuery(id+"F11.wireOp",EDGE,"E137"),sQuery(id+"F11.wireOp",EDGE,"E139"),sQuery(id+"F11.wireOp",EDGE,"E140"),sQuery(id+"F11.wireOp",EDGE,"E141"),sQuery(id+"F11.wireOp",EDGE,"E142")])],"isStart":false})]});
            var sketch = newSketch(context, id + "F13", { "sketchPlane" : qUnion([Q0])});
            skCircle(sketch, "E143", {"center": v(-4, 61) * mm, "radius": 2.5 * mm});
            skSolve(sketch);
        }
        {
            var Q0;
            Q0 = qSketchRegion(id + "F13", true);
            extrude(context, id + "F14", {"entities" : qUnion([Q0]), "operationType" : NewBodyOperationType.REMOVE, "oppositeDirection" : true, "depth" : 5 * mm, "offsetDistance" : 25 * mm});
        }
        {
            var Q0;
            Q0=qCreatedBy(makeId("Right.planeOp"),FACE);
            cPlane(context, id + "F15", {"entities" : qUnion([Q0]), "cplaneType" : CPlaneType.OFFSET, "offset" : 5 * mm, "width" : 150 * mm, "height" : 150 * mm});
        }
        {
            var Q0;
            Q0=qCreatedBy(id+"F15.planeOp",FACE);
            var sketch = newSketch(context, id + "F16", { "sketchPlane" : qUnion([Q0])});
            skLineSegment(sketch, "E144.bottom", {"start": v(35, 4) * mm, "end": v(59, 4) * mm});
            skLineSegment(sketch, "E144.top", {"start": v(35, 1) * mm, "end": v(59, 1) * mm});
            skLineSegment(sketch, "E144.left", {"start": v(35, 4) * mm, "end": v(35, 1) * mm});
            skLineSegment(sketch, "E144.right", {"start": v(59, 4) * mm, "end": v(59, 1) * mm});
            skSolve(sketch);
        }
        {
            var Q0;
            Q0 = qSketchRegion(id + "F16", true);
            extrude(context, id + "F17", {"entities" : qUnion([Q0]), "operationType" : NewBodyOperationType.REMOVE, "oppositeDirection" : true, "depth" : 25 * mm, "offsetDistance" : 25 * mm});
        }
        {
            var Q0;
            Q0=qCreatedBy(makeId("Top.planeOp"),FACE);
            var sketch = newSketch(context, id + "F18", { "sketchPlane" : qUnion([Q0])});
            skLineSegment(sketch, "E145.bottom", {"start": v(-6.46, -6.34) * mm, "end": v(72.54, -6.34) * mm});
            skLineSegment(sketch, "E145.top", {"start": v(-6.46, -60.34) * mm, "end": v(72.54, -60.34) * mm});
            skLineSegment(sketch, "E145.left", {"start": v(-9.46, -9.34) * mm, "end": v(-9.46, -57.34) * mm});
            skLineSegment(sketch, "E145.right", {"start": v(75.54, -9.34) * mm, "end": v(75.54, -57.34) * mm});
            skPoint(sketch, "E146.visualSharp", {"position": v(-9.46, -6.34) * mm});
            skArc(sketch, "E146.filletArc", {"start": v(-6.46, -6.34) * mm, "mid": v(-8.58, -7.22) * mm, "end": v(-9.46, -9.34) * mm});
            skPoint(sketch, "E147.visualSharp", {"position": v(75.54, -6.34) * mm});
            skArc(sketch, "E147.filletArc", {"start": v(75.54, -9.34) * mm, "mid": v(74.66, -7.22) * mm, "end": v(72.54, -6.34) * mm});
            skPoint(sketch, "E148.visualSharp", {"position": v(75.54, -60.34) * mm});
            skArc(sketch, "E148.filletArc", {"start": v(72.54, -60.34) * mm, "mid": v(74.66, -59.46) * mm, "end": v(75.54, -57.34) * mm});
            skPoint(sketch, "E149.visualSharp", {"position": v(-9.46, -60.34) * mm});
            skArc(sketch, "E149.filletArc", {"start": v(-9.46, -57.34) * mm, "mid": v(-8.58, -59.46) * mm, "end": v(-6.46, -60.34) * mm});
            skSolve(sketch);
        }
        {
            var Q0;
            Q0 = qSketchRegion(id + "F18", true);
            extrude(context, id + "F19", {"entities" : qUnion([Q0]), "depth" : 1 * mm, "offsetDistance" : 25 * mm});
        }
    });
